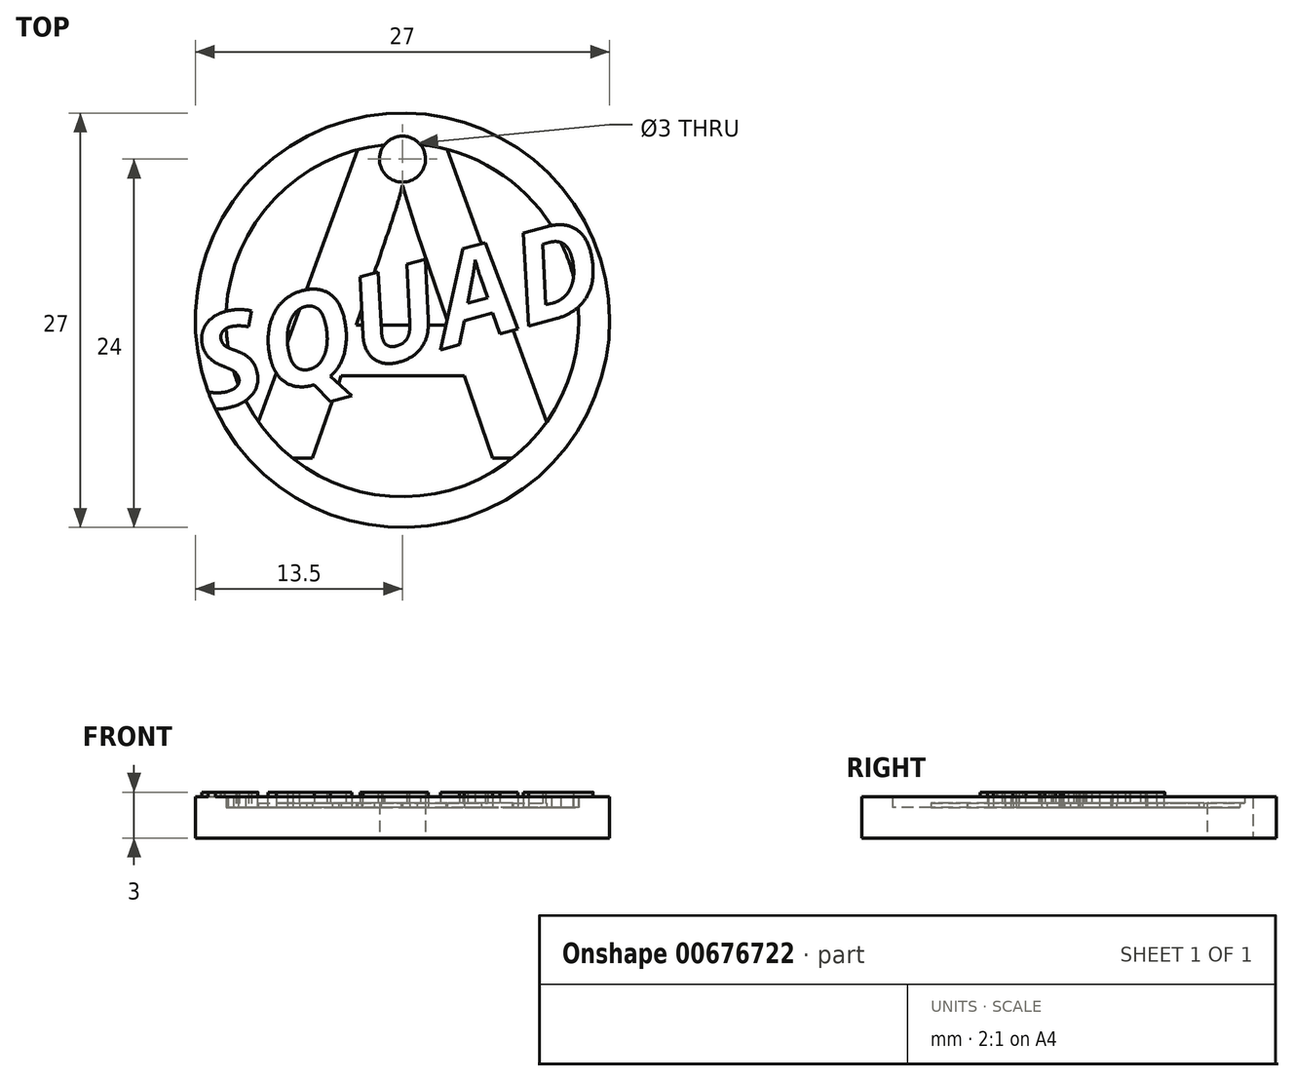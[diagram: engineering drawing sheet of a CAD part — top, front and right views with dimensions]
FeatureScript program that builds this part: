
annotation { "Feature Type Name" : "Feature", "Feature Type Description" : "" }
export const myFeature = defineFeature(function(context is Context, id is Id, definition is map)
    precondition{}
    {
        {
            var Q0;
            Q0=qCreatedBy(makeId("Top.planeOp"),FACE);
            var sketch = newSketch(context, id + "F0", { "sketchPlane" : qUnion([Q0])});
            skText(sketch, "E0", { "text": "A", "fontName": "Arimo-Bold.ttf"});
            skText(sketch, "E1", { "text": "SQUAD", "fontName": "OpenSans-BoldItalic.ttf"});
            skLineSegment(sketch, "E2", {"start": v(0, 45.1) * mm, "end": v(0, -29.18) * mm, "construction": true});
            skCircle(sketch, "E3", {"center": v(-12.24, 15.5) * mm, "radius": 1.5 * mm});
            skLineSegment(sketch, "E4", {"start": v(-12.24, 15.5) * mm, "end": v(-12.24, -11.45) * mm, "construction": true});
            skCircle(sketch, "E5", {"center": v(-12.24, 5) * mm, "radius": 11.5 * mm});
            skCircle(sketch, "E6.0", {"center": v(-12.24, 5) * mm, "radius": 13.5 * mm});
            const initialGuessF0  = {"E0": [-0.02326, -0.004, 1, 0, 0.022], "E1": [-0.025, -0.001, 0.96593, 0.25882, 0.006]};
            skSetInitialGuess(sketch, initialGuessF0);
            skSolve(sketch);
        }
        {
            var Q0;
            {var subQ12=sQuery(id+"F0.wireOp",EDGE,"E0.sketch_text.stroke-5");Q0=makeQuery(id+"F0.imprint","IMPRINT",FACE,{"disambiguationData":[TD([[makeQuery(id+"F0.imprint","IMPRINT",EDGE,{"derivedFrom":subQ12}),1.0]])]});}
            var Q1;
            {var subQ1=sQuery(id+"F0.wireOp",EDGE,"E0.sketch_text.stroke-4");var subQ7=sQuery(id+"F0.wireOp",EDGE,"E6.0");var subQ9=makeQuery(id+"F0.imprint","INTERSECT",VERTEX,{"derivedFrom":[subQ1,subQ7]});Q1=makeQuery(id+"F0.imprint","IMPRINT",FACE,{"disambiguationData":[TD([[makeQuery(id+"F0.imprint","IMPRINT",EDGE,{"disambiguationData":[TD([[subQ9,-1.0]])],"derivedFrom":subQ1}),1.0]])]});}
            var Q2;
            {var subQ0=sQuery(id+"F0.wireOp",EDGE,"E6.0");var subQ1=sQuery(id+"F0.wireOp",EDGE,"E0.sketch_text.stroke-3");var subQ2=makeQuery(id+"F0.imprint","INTERSECT",VERTEX,{"derivedFrom":[subQ1,subQ0]});Q2=makeQuery(id+"F0.imprint","IMPRINT",FACE,{"disambiguationData":[TD([[makeQuery(id+"F0.imprint","IMPRINT",EDGE,{"disambiguationData":[TD([[subQ2,1.0]])],"derivedFrom":subQ1}),-1.0]])]});}
            var Q3;
            {var subQ0=sQuery(id+"F0.wireOp",EDGE,"E6.0");var subQ1=sQuery(id+"F0.wireOp",EDGE,"E0.sketch_text.stroke-3");var subQ2=makeQuery(id+"F0.imprint","INTERSECT",VERTEX,{"derivedFrom":[subQ1,subQ0]});Q3=makeQuery(id+"F0.imprint","IMPRINT",FACE,{"disambiguationData":[TD([[makeQuery(id+"F0.imprint","IMPRINT",EDGE,{"disambiguationData":[TD([[subQ2,1.0]])],"derivedFrom":subQ1}),1.0]])]});}
            var Q4;
            {var subQ0=sQuery(id+"F0.wireOp",EDGE,"E6.0");var subQ1=sQuery(id+"F0.wireOp",EDGE,"E0.sketch_text.stroke-6");var subQ2=makeQuery(id+"F0.imprint","INTERSECT",VERTEX,{"derivedFrom":[subQ1,subQ0]});Q4=makeQuery(id+"F0.imprint","IMPRINT",FACE,{"disambiguationData":[TD([[makeQuery(id+"F0.imprint","IMPRINT",EDGE,{"disambiguationData":[TD([[subQ2,1.0]])],"derivedFrom":subQ1}),-1.0]])]});}
            var Q5;
            {var subQ1=sQuery(id+"F0.wireOp",EDGE,"E0.sketch_text.stroke-5");Q5=makeQuery(id+"F0.imprint","IMPRINT",FACE,{"disambiguationData":[TD([[makeQuery(id+"F0.imprint","IMPRINT",EDGE,{"derivedFrom":subQ1}),-1.0]])]});}
            var Q6;
            {var subQ4=sQuery(id+"F0.wireOp",EDGE,"E1.sketch_text.stroke-19");Q6=makeQuery(id+"F0.imprint","IMPRINT",FACE,{"disambiguationData":[TD([[makeQuery(id+"F0.imprint","IMPRINT",EDGE,{"derivedFrom":subQ4}),1.0]])]});}
            var Q7;
            {var subQ0=sQuery(id+"F0.wireOp",EDGE,"E1.sketch_text.stroke-87");Q7=makeQuery(id+"F0.imprint","IMPRINT",FACE,{"disambiguationData":[TD([[makeQuery(id+"F0.imprint","IMPRINT",EDGE,{"derivedFrom":subQ0}),1.0]])]});}
            extrude(context, id + "F1", {"entities" : qUnion([Q0, Q1, Q2, Q3, Q4, Q5, Q6, Q7]), "depth" : 2.7 * mm, "offsetDistance" : 25 * mm});
        }
        {
            var Q0;
            {var subQ11=sQuery(id+"F0.wireOp",EDGE,"E1.sketch_text.stroke-0");Q0=makeQuery(id+"F0.imprint","IMPRINT",FACE,{"disambiguationData":[TD([[makeQuery(id+"F0.imprint","IMPRINT",EDGE,{"derivedFrom":subQ11}),1.0]])]});}
            var Q1;
            {var subQ12=sQuery(id+"F0.wireOp",EDGE,"E0.sketch_text.stroke-0");Q1=makeQuery(id+"F0.imprint","IMPRINT",FACE,{"disambiguationData":[TD([[makeQuery(id+"F0.imprint","IMPRINT",EDGE,{"derivedFrom":subQ12}),1.0]])]});}
            var Q2;
            {var subQ8=sQuery(id+"F0.wireOp",EDGE,"E1.sketch_text.stroke-67");Q2=makeQuery(id+"F0.imprint","IMPRINT",FACE,{"disambiguationData":[TD([[makeQuery(id+"F0.imprint","IMPRINT",EDGE,{"derivedFrom":subQ8}),1.0]])]});}
            var Q3;
            Q3=makeQuery(id+"F0.imprint","IMPRINT",FACE,{"disambiguationData":[TD([[makeQuery(id+"F0.imprint","IMPRINT",EDGE,{"derivedFrom":sQuery(id+"F0.wireOp",EDGE,"E0.sketch_text.stroke-8")}),1.0]])]});
            var Q4;
            {var subQ0=sQuery(id+"F0.wireOp",EDGE,"E0.sketch_text.stroke-11");var subQ1=sQuery(id+"F0.wireOp",EDGE,"E0.sketch_text.stroke-10");var subQ2=makeQuery(id+"F0.imprint","INTERSECT",VERTEX,{"derivedFrom":[subQ1,subQ0]});Q4=makeQuery(id+"F0.imprint","IMPRINT",FACE,{"disambiguationData":[TD([[makeQuery(id+"F0.imprint","IMPRINT",EDGE,{"disambiguationData":[TD([[subQ2,1.0]])],"derivedFrom":subQ1}),1.0]])]});}
            var Q5;
            {var subQ0=sQuery(id+"F0.wireOp",EDGE,"E1.sketch_text.stroke-7");Q5=makeQuery(id+"F0.imprint","IMPRINT",FACE,{"disambiguationData":[TD([[makeQuery(id+"F0.imprint","IMPRINT",EDGE,{"derivedFrom":subQ0}),1.0]])]});}
            var Q6;
            {var subQ5=sQuery(id+"F0.wireOp",EDGE,"E1.sketch_text.stroke-38");Q6=makeQuery(id+"F0.imprint","IMPRINT",FACE,{"disambiguationData":[TD([[makeQuery(id+"F0.imprint","IMPRINT",EDGE,{"derivedFrom":subQ5}),1.0]])]});}
            var Q7;
            Q7=makeQuery(id+"F0.imprint","IMPRINT",FACE,{"disambiguationData":[TD([[makeQuery(id+"F0.imprint","IMPRINT",EDGE,{"derivedFrom":sQuery(id+"F0.wireOp",EDGE,"E1.sketch_text.stroke-84")}),1.0]])]});
            extrude(context, id + "F2", {"entities" : qUnion([Q0, Q1, Q2, Q3, Q4, Q5, Q6, Q7]), "operationType" : NewBodyOperationType.ADD, "depth" : 2 * mm, "offsetDistance" : 25 * mm});
        }
        {
            var Q0;
            {var subQ41=sQuery(id+"F0.wireOp",EDGE,"E0.sketch_text.stroke-0");Q0=makeQuery(id+"F0.imprint","IMPRINT",FACE,{"disambiguationData":[TD([[makeQuery(id+"F0.imprint","IMPRINT",EDGE,{"derivedFrom":subQ41}),-1.0]])]});}
            var Q1;
            {var subQ0=sQuery(id+"F0.wireOp",EDGE,"E1.sketch_text.stroke-28");Q1=makeQuery(id+"F0.imprint","IMPRINT",FACE,{"disambiguationData":[TD([[makeQuery(id+"F0.imprint","IMPRINT",EDGE,{"derivedFrom":subQ0}),1.0]])]});}
            var Q2;
            {var subQ0=sQuery(id+"F0.wireOp",EDGE,"E1.sketch_text.stroke-40");Q2=makeQuery(id+"F0.imprint","IMPRINT",FACE,{"disambiguationData":[TD([[makeQuery(id+"F0.imprint","IMPRINT",EDGE,{"derivedFrom":subQ0}),1.0]])]});}
            var Q3;
            Q3=makeQuery(id+"F0.imprint","IMPRINT",FACE,{"disambiguationData":[TD([[makeQuery(id+"F0.imprint","IMPRINT",EDGE,{"derivedFrom":sQuery(id+"F0.wireOp",EDGE,"E1.sketch_text.stroke-70")}),1.0]])]});
            var Q4;
            {var subQ0=sQuery(id+"F0.wireOp",EDGE,"E1.sketch_text.stroke-56");Q4=makeQuery(id+"F0.imprint","IMPRINT",FACE,{"disambiguationData":[TD([[makeQuery(id+"F0.imprint","IMPRINT",EDGE,{"derivedFrom":subQ0}),1.0]])]});}
            extrude(context, id + "F3", {"entities" : qUnion([Q0, Q1, Q2, Q3, Q4]), "operationType" : NewBodyOperationType.ADD, "depth" : 2.3 * mm, "offsetDistance" : 25 * mm});
        }
        {
            var Q0;
            {var subQ8=sQuery(id+"F0.wireOp",EDGE,"E1.sketch_text.stroke-9");Q0=makeQuery(id+"F0.imprint","IMPRINT",FACE,{"disambiguationData":[TD([[makeQuery(id+"F0.imprint","IMPRINT",EDGE,{"derivedFrom":subQ8}),-1.0]])]});}
            var Q1;
            {var subQ4=sQuery(id+"F0.wireOp",EDGE,"E1.sketch_text.stroke-16");Q1=makeQuery(id+"F0.imprint","IMPRINT",FACE,{"disambiguationData":[TD([[makeQuery(id+"F0.imprint","IMPRINT",EDGE,{"derivedFrom":subQ4}),-1.0]])]});}
            var Q2;
            {var subQ1=sQuery(id+"F0.wireOp",EDGE,"E1.sketch_text.stroke-0");Q2=makeQuery(id+"F0.imprint","IMPRINT",FACE,{"disambiguationData":[TD([[makeQuery(id+"F0.imprint","IMPRINT",EDGE,{"derivedFrom":subQ1}),-1.0]])]});}
            var Q3;
            {var subQ0=sQuery(id+"F0.wireOp",EDGE,"E1.sketch_text.stroke-5");Q3=makeQuery(id+"F0.imprint","IMPRINT",FACE,{"disambiguationData":[TD([[makeQuery(id+"F0.imprint","IMPRINT",EDGE,{"derivedFrom":subQ0}),-1.0]])]});}
            var Q4;
            Q4=makeQuery(id+"F0.imprint","IMPRINT",FACE,{"disambiguationData":[TD([[makeQuery(id+"F0.imprint","IMPRINT",EDGE,{"derivedFrom":sQuery(id+"F0.wireOp",EDGE,"E1.sketch_text.stroke-24")}),-1.0]])]});
            var Q5;
            {var subQ0=sQuery(id+"F0.wireOp",EDGE,"E1.sketch_text.stroke-26");var subQ1=sQuery(id+"F0.wireOp",EDGE,"E0.sketch_text.stroke-2");var subQ2=makeQuery(id+"F0.imprint","INTERSECT",VERTEX,{"derivedFrom":[subQ1,subQ0]});Q5=makeQuery(id+"F0.imprint","IMPRINT",FACE,{"disambiguationData":[TD([[makeQuery(id+"F0.imprint","IMPRINT",EDGE,{"disambiguationData":[TD([[subQ2,-1.0]])],"derivedFrom":subQ1}),1.0]])]});}
            var Q6;
            {var subQ0=sQuery(id+"F0.wireOp",EDGE,"E1.sketch_text.stroke-32");Q6=makeQuery(id+"F0.imprint","IMPRINT",FACE,{"disambiguationData":[TD([[makeQuery(id+"F0.imprint","IMPRINT",EDGE,{"derivedFrom":subQ0}),-1.0]])]});}
            var Q7;
            {var subQ0=sQuery(id+"F0.wireOp",EDGE,"E1.sketch_text.stroke-54");var subQ1=sQuery(id+"F0.wireOp",EDGE,"E0.sketch_text.stroke-10");var subQ2=makeQuery(id+"F0.imprint","INTERSECT",VERTEX,{"derivedFrom":[subQ1,subQ0]});Q7=makeQuery(id+"F0.imprint","IMPRINT",FACE,{"disambiguationData":[TD([[makeQuery(id+"F0.imprint","IMPRINT",EDGE,{"disambiguationData":[TD([[subQ2,-1.0]])],"derivedFrom":subQ1}),-1.0]])]});}
            var Q8;
            {var subQ1=sQuery(id+"F0.wireOp",EDGE,"E1.sketch_text.stroke-54");var subQ3=sQuery(id+"F0.wireOp",EDGE,"E0.sketch_text.stroke-10");var subQ4=makeQuery(id+"F0.imprint","INTERSECT",VERTEX,{"derivedFrom":[subQ3,subQ1]});Q8=makeQuery(id+"F0.imprint","IMPRINT",FACE,{"disambiguationData":[TD([[makeQuery(id+"F0.imprint","IMPRINT",EDGE,{"disambiguationData":[TD([[subQ4,-1.0]])],"derivedFrom":subQ3}),1.0]])]});}
            var Q9;
            {var subQ11=sQuery(id+"F0.wireOp",EDGE,"E1.sketch_text.stroke-49");Q9=makeQuery(id+"F0.imprint","IMPRINT",FACE,{"disambiguationData":[TD([[makeQuery(id+"F0.imprint","IMPRINT",EDGE,{"derivedFrom":subQ11}),-1.0]])]});}
            var Q10;
            {var subQ5=sQuery(id+"F0.wireOp",EDGE,"E1.sketch_text.stroke-47");Q10=makeQuery(id+"F0.imprint","IMPRINT",FACE,{"disambiguationData":[TD([[makeQuery(id+"F0.imprint","IMPRINT",EDGE,{"derivedFrom":subQ5}),-1.0]])]});}
            var Q11;
            {var subQ0=sQuery(id+"F0.wireOp",EDGE,"E0.sketch_text.stroke-12");var subQ1=sQuery(id+"F0.wireOp",EDGE,"E0.sketch_text.stroke-11");var subQ2=makeQuery(id+"F0.imprint","INTERSECT",VERTEX,{"derivedFrom":[subQ1,subQ0]});Q11=makeQuery(id+"F0.imprint","IMPRINT",FACE,{"disambiguationData":[TD([[makeQuery(id+"F0.imprint","IMPRINT",EDGE,{"disambiguationData":[TD([[subQ2,1.0]])],"derivedFrom":subQ1}),1.0]])]});}
            var Q12;
            Q12=makeQuery(id+"F0.imprint","IMPRINT",FACE,{"disambiguationData":[TD([[makeQuery(id+"F0.imprint","IMPRINT",EDGE,{"derivedFrom":sQuery(id+"F0.wireOp",EDGE,"E1.sketch_text.stroke-62")}),-1.0]])]});
            var Q13;
            {var subQ5=sQuery(id+"F0.wireOp",EDGE,"E1.sketch_text.stroke-67");Q13=makeQuery(id+"F0.imprint","IMPRINT",FACE,{"disambiguationData":[TD([[makeQuery(id+"F0.imprint","IMPRINT",EDGE,{"derivedFrom":subQ5}),-1.0]])]});}
            var Q14;
            {var subQ7=sQuery(id+"F0.wireOp",EDGE,"E1.sketch_text.stroke-79");Q14=makeQuery(id+"F0.imprint","IMPRINT",FACE,{"disambiguationData":[TD([[makeQuery(id+"F0.imprint","IMPRINT",EDGE,{"derivedFrom":subQ7}),-1.0]])]});}
            var Q15;
            Q15=makeQuery(id+"F0.imprint","IMPRINT",FACE,{"disambiguationData":[TD([[makeQuery(id+"F0.imprint","IMPRINT",EDGE,{"derivedFrom":sQuery(id+"F0.wireOp",EDGE,"E1.sketch_text.stroke-76")}),-1.0]])]});
            extrude(context, id + "F4", {"entities" : qUnion([Q0, Q1, Q2, Q3, Q4, Q5, Q6, Q7, Q8, Q9, Q10, Q11, Q12, Q13, Q14, Q15]), "operationType" : NewBodyOperationType.ADD, "depth" : 3 * mm, "offsetDistance" : 25 * mm});
        }
    });
